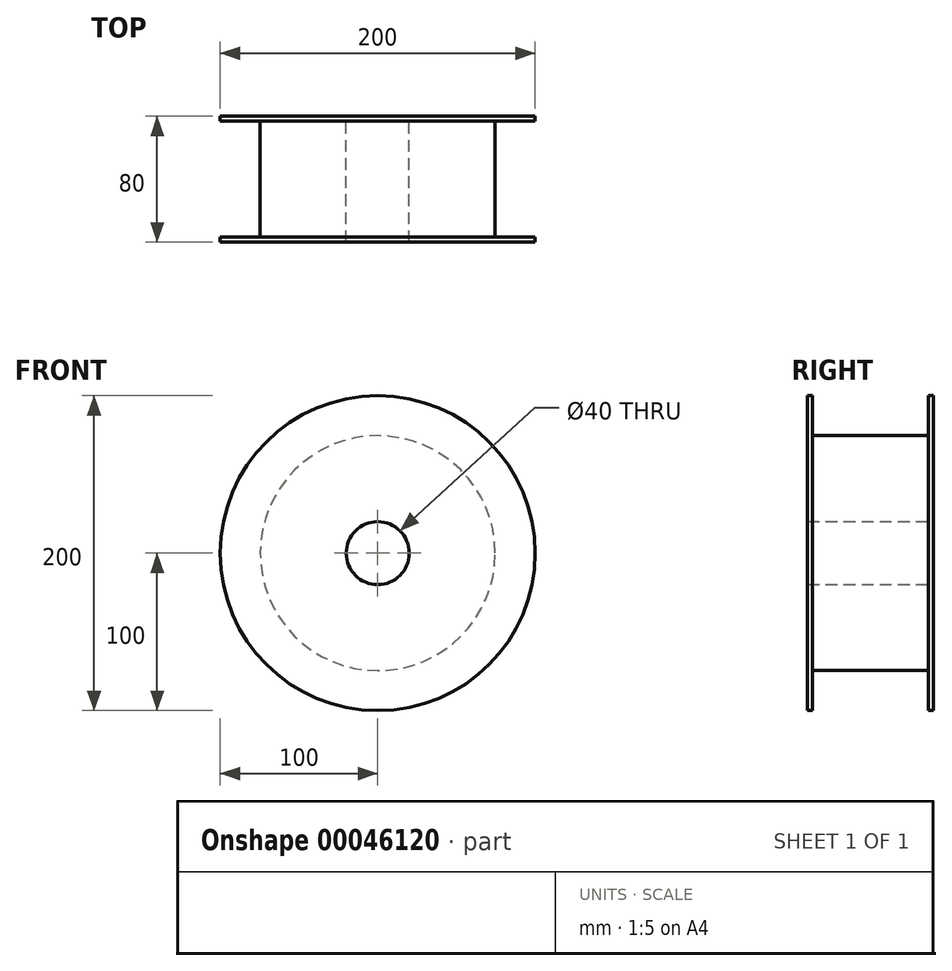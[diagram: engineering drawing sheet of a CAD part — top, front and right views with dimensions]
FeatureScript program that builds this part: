
annotation { "Feature Type Name" : "Feature", "Feature Type Description" : "" }
export const myFeature = defineFeature(function(context is Context, id is Id, definition is map)
    precondition{}
    {
        {
            var Q0;
            Q0=qCreatedBy(makeId("Front.planeOp"),FACE);
            var sketch = newSketch(context, id + "F0", { "sketchPlane" : qUnion([Q0])});
            skCircle(sketch, "E0", {"center": v(0, 0) * mm, "radius": 100 * mm});
            skCircle(sketch, "E1", {"center": v(0, 0) * mm, "radius": 20 * mm});
            skCircle(sketch, "E2", {"center": v(0, 0) * mm, "radius": 74.6 * mm});
            skSolve(sketch);
        }
        {
            var Q0;
            Q0=makeQuery(id+"F0.imprint","IMPRINT",FACE,{"disambiguationData":[TD([[makeQuery(id+"F0.imprint","IMPRINT",EDGE,{"derivedFrom":sQuery(id+"F0.wireOp",EDGE,"E1")}),-1.0]])]});
            var Q1;
            Q1=makeQuery(id+"F0.imprint","IMPRINT",FACE,{"disambiguationData":[TD([[makeQuery(id+"F0.imprint","IMPRINT",EDGE,{"derivedFrom":sQuery(id+"F0.wireOp",EDGE,"E0")}),1.0]])]});
            extrude(context, id + "F1", {"entities" : qUnion([Q0, Q1]), "depth" : 80 * mm});
        }
        {
            var Q0;
            Q0=makeQuery(id+"F0.imprint","IMPRINT",FACE,{"disambiguationData":[TD([[makeQuery(id+"F0.imprint","IMPRINT",EDGE,{"derivedFrom":sQuery(id+"F0.wireOp",EDGE,"E0")}),1.0]])]});
            extrude(context, id + "F2", {"entities" : qUnion([Q0]), "operationType" : NewBodyOperationType.REMOVE, "depth" : 76.83 * mm, "hasSecondDirection" : true, "secondDirectionOppositeDirection" : false, "secondDirectionDepth" : 3.17 * mm});
        }
    });
